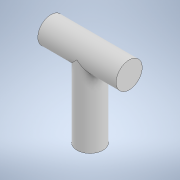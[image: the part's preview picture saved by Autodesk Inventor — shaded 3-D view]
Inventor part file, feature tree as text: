
AUTODESK INVENTOR PART (.ipt)
format: ipt  version: 2021 (Build 250183000, 183)  size: 103,936 bytes
history: native  units: in
note: dims shown in document units (in); Inventor stores cm internally (conversion verified against a paired STEP export)
features: extrude x2, sketch x2
ambient origin geometry x8: Origin, YZ Plane, XZ Plane, XY Plane, X Axis, Y Axis, Z Axis, Center Point
bodies: Solid1 (feature_tree)
feature tree (4):
  extrude  "Extrusion1"  Depth=3.0in TaperAngle=0.0deg
  extrude  "Extrusion2"  Depth=3.0in TaperAngle=0.0deg
  sketch  "Sketch1"  dims[d0=1.0in d1=3.0in d2=0.0in]
  sketch  "Sketch2"  dims[d3=1.0in d4=3.0in d5=0.0in]
